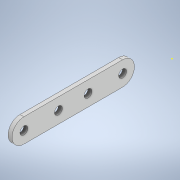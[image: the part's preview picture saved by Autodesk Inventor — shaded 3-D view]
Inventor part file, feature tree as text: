
AUTODESK INVENTOR PART (.ipt)
format: ipt  version: 2021 (Build 250183000, 183)  size: 155,136 bytes
history: native  units: mm
features: sketch x4, extrude x3, fillet x1
ambient origin geometry x8: Origin, YZ Plane, XZ Plane, XY Plane, X Axis, Y Axis, Z Axis, Center Point
bodies: Solid1 (feature_tree)
feature tree (8):
  extrude  "Extrusion1"  Depth=24.0mm
  fillet  "Fillet1"  Radius=200.0mm
  extrude  "Extrusion2"  Depth=8.0mm
  sketch  "Sketch3"  dims[d6=8.0mm d7=10.0mm d8=0.0mm]
  extrude  "Extrusion4"  Depth=10.0mm TaperAngle=0.0deg
  sketch  "Sketch1"  dims[d0=4.0mm d1=24.0mm d2=200.0mm d3=0.0mm]
  sketch  "Sketch2"  dims[d4=5.0mm d5=8.0mm]
  sketch  "Sketch4"  dims[d9=50.0mm d10=50.0mm d11=12.0mm d12=12.0mm d13=8.0mm d14=8.0mm d15=8.0mm d16=8.0mm d17=25.0mm d18=25.0mm d19=85.0mm d20=85.0mm d23=10.0mm d24=0.0mm]
